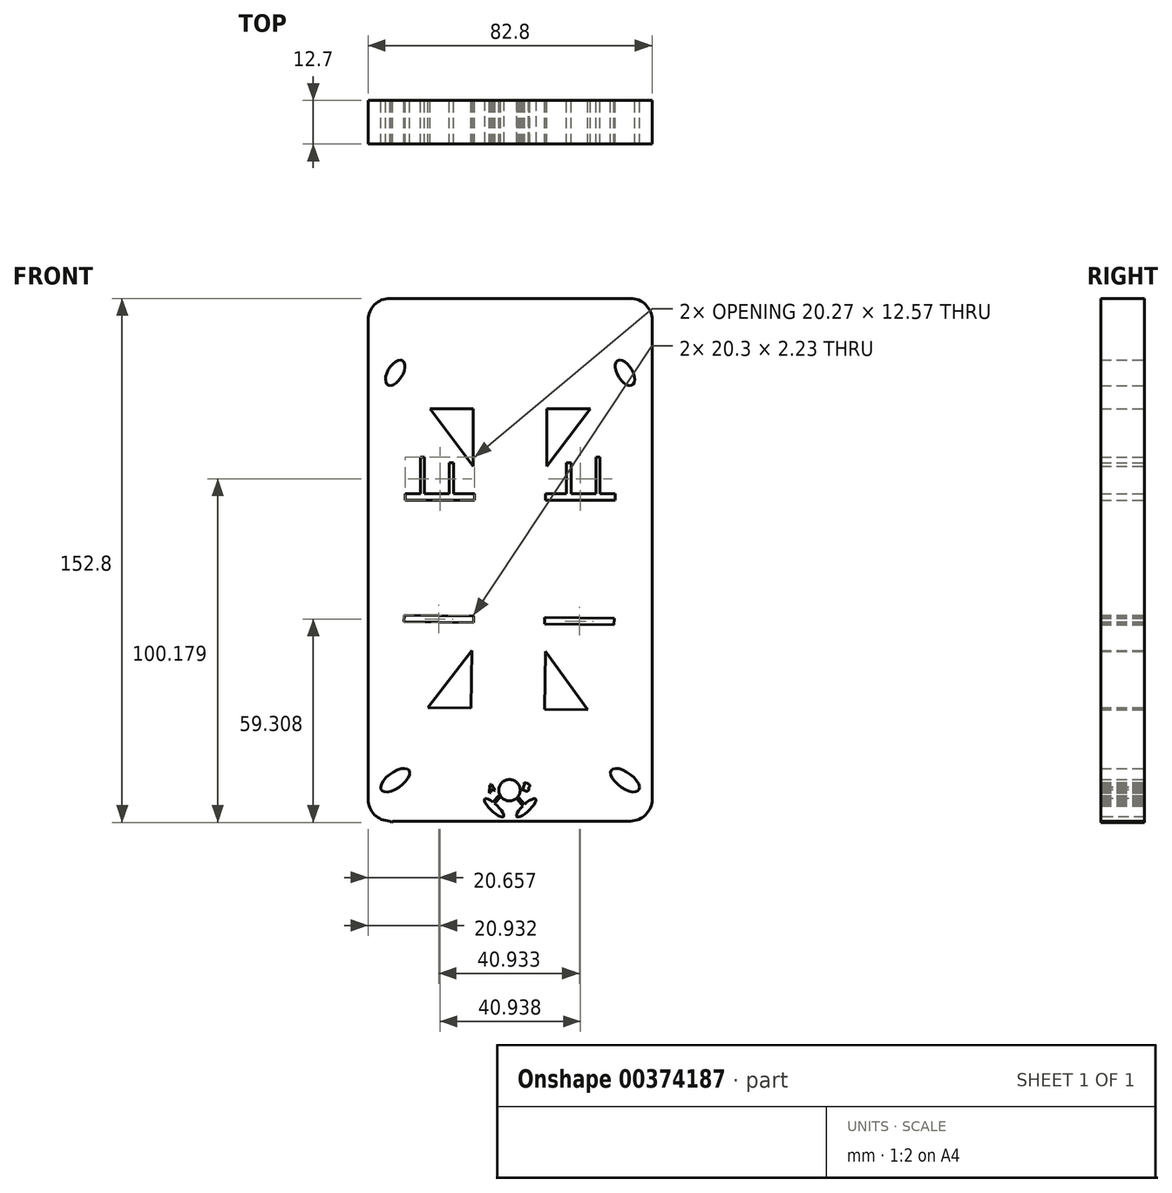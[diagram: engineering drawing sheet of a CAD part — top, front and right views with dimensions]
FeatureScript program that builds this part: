
annotation { "Feature Type Name" : "Feature", "Feature Type Description" : "" }
export const myFeature = defineFeature(function(context is Context, id is Id, definition is map)
    precondition{}
    {
        {
            var Q0;
            Q0=qCreatedBy(makeId("Front.planeOp"),FACE);
            var sketch = newSketch(context, id + "F0", { "sketchPlane" : qUnion([Q0])});
            skLineSegment(sketch, "E0.bottom", {"start": v(-34.85, 75.56) * mm, "end": v(35.25, 75.56) * mm});
            skLineSegment(sketch, "E0.top", {"start": v(-34.85, -76.84) * mm, "end": v(35.25, -76.84) * mm});
            skLineSegment(sketch, "E0.left", {"start": v(-41.2, 69.21) * mm, "end": v(-41.2, -70.49) * mm});
            skLineSegment(sketch, "E0.right", {"start": v(41.6, 69.21) * mm, "end": v(41.6, -70.49) * mm});
            skPoint(sketch, "E1.visualSharp", {"position": v(-41.2, 75.56) * mm});
            skArc(sketch, "E1.filletArc", {"start": v(-34.85, 75.56) * mm, "mid": v(-39.34, 73.7) * mm, "end": v(-41.2, 69.21) * mm});
            skPoint(sketch, "E2.visualSharp", {"position": v(41.6, 75.56) * mm});
            skArc(sketch, "E2.filletArc", {"start": v(41.6, 69.21) * mm, "mid": v(39.74, 73.7) * mm, "end": v(35.25, 75.56) * mm});
            skPoint(sketch, "E3.visualSharp", {"position": v(-41.2, -76.84) * mm});
            skArc(sketch, "E3.filletArc", {"start": v(-41.2, -70.49) * mm, "mid": v(-39.34, -74.98) * mm, "end": v(-34.85, -76.84) * mm});
            skPoint(sketch, "E4.visualSharp", {"position": v(41.6, -76.84) * mm});
            skArc(sketch, "E4.filletArc", {"start": v(35.25, -76.84) * mm, "mid": v(39.74, -74.98) * mm, "end": v(41.6, -70.49) * mm});
            skEllipse(sketch, "E5", {"center": v(-33.29, 53.84) * mm, "majorRadius": 4.13 * mm, "minorRadius": 2.18 * mm, "majorAxis": v(0.52, 0.85)});
            skEllipse(sketch, "E6", {"center": v(-33.29, -64.92) * mm, "majorRadius": 4.95 * mm, "minorRadius": 2.3 * mm, "majorAxis": v(0.81, 0.58)});
            skEllipse(sketch, "E7.MirrorC", {"center": v(33.69, -64.92) * mm, "majorRadius": 4.95 * mm, "minorRadius": 2.3 * mm, "majorAxis": v(-0.81, 0.58)});
            skEllipse(sketch, "E8.MirrorC", {"center": v(33.69, 53.84) * mm, "majorRadius": 4.13 * mm, "minorRadius": 2.18 * mm, "majorAxis": v(-0.52, 0.85)});
            skLineSegment(sketch, "E9", {"start": v(-23.14, 43.43) * mm, "end": v(-10.51, 43.43) * mm});
            skLineSegment(sketch, "E10", {"start": v(-10.51, 43.43) * mm, "end": v(-10.51, 26.6) * mm});
            skLineSegment(sketch, "E11", {"start": v(-10.51, 26.6) * mm, "end": v(-23.14, 43.43) * mm});
            skLineSegment(sketch, "E12.MirrorCS", {"start": v(10.92, 43.43) * mm, "end": v(10.92, 26.6) * mm});
            skLineSegment(sketch, "E13.MirrorCS", {"start": v(23.54, 43.43) * mm, "end": v(10.92, 43.43) * mm});
            skLineSegment(sketch, "E14.MirrorCS", {"start": v(10.92, 26.6) * mm, "end": v(23.54, 43.43) * mm});
            skLineSegment(sketch, "E15", {"start": v(-41.2, 0) * mm, "end": v(41.6, -0.64) * mm});
            skPoint(sketch, "E15.startSnap0", {"position": v(-41.2, -0.64) * mm});
            skLineSegment(sketch, "E16.MirrorCS", {"start": v(-10.93, -27.07) * mm, "end": v(-23.81, -43.7) * mm});
            skLineSegment(sketch, "E17.MirrorCS", {"start": v(-11.19, -43.9) * mm, "end": v(-10.93, -27.07) * mm});
            skLineSegment(sketch, "E18.MirrorCS", {"start": v(-23.81, -43.7) * mm, "end": v(-11.19, -43.9) * mm});
            skLineSegment(sketch, "E19.MirrorCS", {"start": v(10.24, -44.23) * mm, "end": v(10.5, -27.4) * mm});
            skLineSegment(sketch, "E20.MirrorCS", {"start": v(22.86, -44.42) * mm, "end": v(10.24, -44.23) * mm});
            skLineSegment(sketch, "E21.MirrorCS", {"start": v(10.5, -27.4) * mm, "end": v(22.86, -44.42) * mm});
            skLineSegment(sketch, "E22.bottom", {"start": v(-30.4, 18.57) * mm, "end": v(-10.13, 18.57) * mm});
            skLineSegment(sketch, "E22.top", {"start": v(-30.4, 16.65) * mm, "end": v(-10.13, 16.65) * mm});
            skLineSegment(sketch, "E22.left", {"start": v(-30.4, 18.57) * mm, "end": v(-30.4, 16.65) * mm});
            skLineSegment(sketch, "E22.right", {"start": v(-10.13, 18.57) * mm, "end": v(-10.13, 16.65) * mm});
            skLineSegment(sketch, "E23.MirrorCS", {"start": v(30.8, 16.65) * mm, "end": v(10.53, 16.65) * mm});
            skLineSegment(sketch, "E24.MirrorCS", {"start": v(30.8, 18.57) * mm, "end": v(10.53, 18.57) * mm});
            skLineSegment(sketch, "E25.MirrorCS", {"start": v(10.53, 18.57) * mm, "end": v(10.53, 16.65) * mm});
            skLineSegment(sketch, "E26.MirrorCS", {"start": v(30.8, 18.57) * mm, "end": v(30.8, 16.65) * mm});
            skLineSegment(sketch, "E27.MirrorCS", {"start": v(30.54, -17.76) * mm, "end": v(10.27, -17.45) * mm});
            skLineSegment(sketch, "E28.MirrorCS", {"start": v(30.51, -19.68) * mm, "end": v(30.54, -17.76) * mm});
            skLineSegment(sketch, "E29.MirrorCS", {"start": v(30.51, -19.68) * mm, "end": v(10.24, -19.36) * mm});
            skLineSegment(sketch, "E30.MirrorCS", {"start": v(10.24, -19.36) * mm, "end": v(10.27, -17.45) * mm});
            skLineSegment(sketch, "E31.MirrorCS", {"start": v(-30.7, -18.73) * mm, "end": v(-30.66, -16.82) * mm});
            skLineSegment(sketch, "E32.MirrorCS", {"start": v(-30.7, -18.73) * mm, "end": v(-10.42, -19.04) * mm});
            skLineSegment(sketch, "E33.MirrorCS", {"start": v(-10.42, -19.04) * mm, "end": v(-10.4, -17.13) * mm});
            skLineSegment(sketch, "E34.MirrorCS", {"start": v(-30.66, -16.82) * mm, "end": v(-10.4, -17.13) * mm});
            skLineSegment(sketch, "E35.bottom", {"start": v(-16.23, 18.57) * mm, "end": v(-17.57, 18.57) * mm});
            skLineSegment(sketch, "E35.top", {"start": v(-16.23, 27.6) * mm, "end": v(-17.57, 27.6) * mm});
            skLineSegment(sketch, "E35.left", {"start": v(-16.23, 18.57) * mm, "end": v(-16.23, 27.6) * mm});
            skLineSegment(sketch, "E35.right", {"start": v(-17.57, 18.57) * mm, "end": v(-17.57, 27.6) * mm});
            skLineSegment(sketch, "E36.bottom", {"start": v(-25.98, 18.57) * mm, "end": v(-24.83, 18.57) * mm});
            skLineSegment(sketch, "E36.top", {"start": v(-25.98, 29.22) * mm, "end": v(-24.83, 29.22) * mm});
            skLineSegment(sketch, "E36.left", {"start": v(-25.98, 18.57) * mm, "end": v(-25.98, 29.22) * mm});
            skLineSegment(sketch, "E36.right", {"start": v(-24.83, 18.57) * mm, "end": v(-24.83, 29.22) * mm});
            skLineSegment(sketch, "E37.MirrorCS", {"start": v(16.63, 18.57) * mm, "end": v(16.63, 27.6) * mm});
            skLineSegment(sketch, "E38.MirrorCS", {"start": v(17.97, 18.57) * mm, "end": v(17.97, 27.6) * mm});
            skLineSegment(sketch, "E39.MirrorCS", {"start": v(16.63, 27.6) * mm, "end": v(17.97, 27.6) * mm});
            skLineSegment(sketch, "E40.MirrorCS", {"start": v(25.24, 18.57) * mm, "end": v(25.24, 29.22) * mm});
            skLineSegment(sketch, "E41.MirrorCS", {"start": v(26.38, 18.57) * mm, "end": v(26.38, 29.22) * mm});
            skLineSegment(sketch, "E42.MirrorCS", {"start": v(26.38, 29.22) * mm, "end": v(25.24, 29.22) * mm});
            skEllipse(sketch, "E43", {"center": v(-4.48, -72.98) * mm, "majorRadius": 3.76 * mm, "minorRadius": 1.1 * mm, "majorAxis": v(-0.73, 0.69)});
            skEllipse(sketch, "E44.MirrorC", {"center": v(4.88, -72.98) * mm, "majorRadius": 3.76 * mm, "minorRadius": 1.1 * mm, "majorAxis": v(0.73, 0.69)});
            skCircle(sketch, "E45", {"center": v(0, -67.86) * mm, "radius": 3.12 * mm});
            skLineSegment(sketch, "E46.bottom", {"start": v(2.72, -70.01) * mm, "end": v(4.38, -72) * mm});
            skLineSegment(sketch, "E46.top", {"start": v(2.25, -70.41) * mm, "end": v(3.91, -72.4) * mm});
            skLineSegment(sketch, "E46.left", {"start": v(2.72, -70.01) * mm, "end": v(2.25, -70.41) * mm});
            skLineSegment(sketch, "E46.right", {"start": v(4.38, -72) * mm, "end": v(3.91, -72.4) * mm});
            skLineSegment(sketch, "E47.bottom", {"start": v(-32.71, -75.26) * mm, "end": v(-34.38, -77.24) * mm});
            skLineSegment(sketch, "E47.top", {"start": v(-33.19, -74.86) * mm, "end": v(-34.85, -76.84) * mm});
            skLineSegment(sketch, "E47.left", {"start": v(-32.71, -75.26) * mm, "end": v(-33.19, -74.86) * mm});
            skLineSegment(sketch, "E47.right", {"start": v(-34.38, -77.24) * mm, "end": v(-34.85, -76.84) * mm});
            skLineSegment(sketch, "E48.bottom", {"start": v(-2.62, -69.76) * mm, "end": v(-4.35, -71.69) * mm});
            skLineSegment(sketch, "E48.top", {"start": v(-3.08, -69.35) * mm, "end": v(-4.81, -71.27) * mm});
            skLineSegment(sketch, "E48.left", {"start": v(-2.62, -69.76) * mm, "end": v(-3.08, -69.35) * mm});
            skLineSegment(sketch, "E48.right", {"start": v(-4.35, -71.69) * mm, "end": v(-4.81, -71.27) * mm});
            skText(sketch, "E49", { "text": "A", "fontName": "OpenSans-BoldItalic.ttf"});
            skText(sketch, "E50", { "text": "B", "fontName": "RobotoSlab-Bold.ttf"});
            const initialGuessF0  = {"E49": [-0.00571, -0.06858, 0.9063, 0.42262, 0.0021], "E50": [0.00348, -0.06766, 0.9397, -0.34202, 0.0023]};
            skSetInitialGuess(sketch, initialGuessF0);
            skSolve(sketch);
        }
        {
            var Q0;
            Q0=qSketchRegion(id+"F0",true);
            extrude(context, id + "F1", {"entities" : qUnion([Q0]), "endBound" : BoundingType.SYMMETRIC, "depth" : 12.7 * mm});
        }
    });
